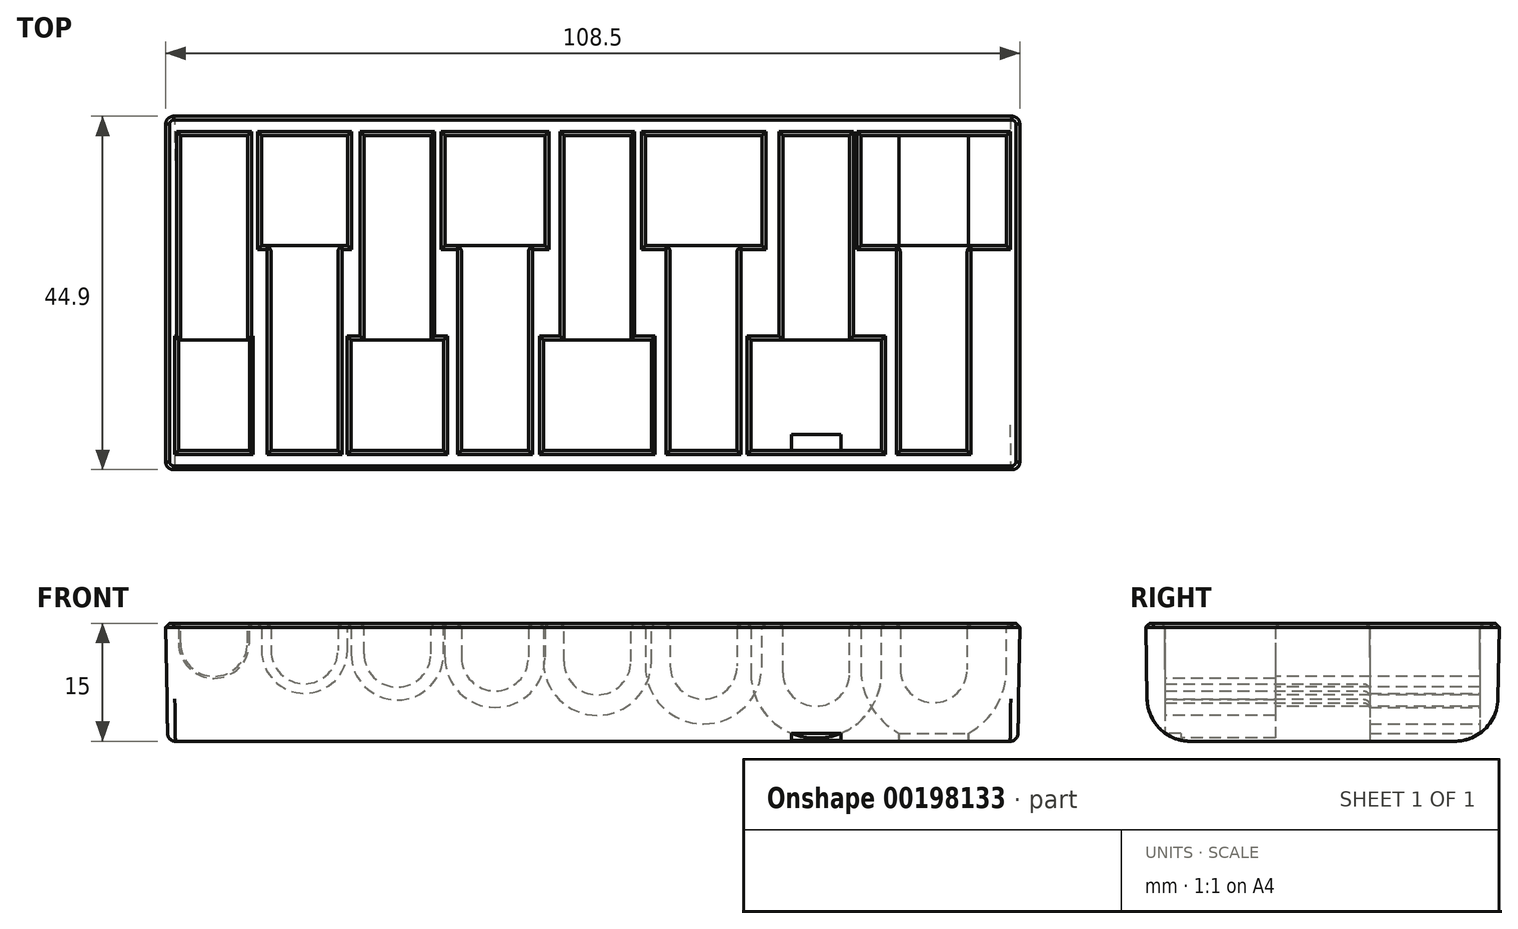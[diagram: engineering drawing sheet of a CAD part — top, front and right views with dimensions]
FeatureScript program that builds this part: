
annotation { "Feature Type Name" : "Feature", "Feature Type Description" : "" }
export const myFeature = defineFeature(function(context is Context, id is Id, definition is map)
    precondition{}
    {
        {
            var Q0;
            Q0=qCreatedBy(makeId("Top.planeOp"),FACE);
            var sketch = newSketch(context, id + "F0", { "sketchPlane" : qUnion([Q0])});
            skLineSegment(sketch, "E0.bottom", {"start": v(54, 22.2) * mm, "end": v(-54, 22.2) * mm});
            skLineSegment(sketch, "E0.top", {"start": v(54, -22.2) * mm, "end": v(-54, -22.2) * mm});
            skLineSegment(sketch, "E0.left", {"start": v(54, 22.2) * mm, "end": v(54, -22.2) * mm});
            skLineSegment(sketch, "E0.right", {"start": v(-54, 22.2) * mm, "end": v(-54, -22.2) * mm});
            skPoint(sketch, "E0.middle", {"position": v(0, 0) * mm});
            skSolve(sketch);
        }
        {
            var Q0;
            Q0=makeQuery(id+"F0.imprint","IMPRINT",FACE,{"disambiguationData":[TD([[makeQuery(id+"F0.imprint","IMPRINT",EDGE,{"derivedFrom":sQuery(id+"F0.wireOp",EDGE,"E0.bottom")}),1.0]])]});
            extrude(context, id + "F1", {"entities" : qUnion([Q0]), "depth" : 15 * mm, "hasDraft" : true, "draftAngle" : 1 * degree});
        }
        {
            var Q0;
            Q0=makeQuery(id+"F1.opExtrude","CAP_EDGE",EDGE,{"disambiguationData":[OSD([sQuery(id+"F0.wireOp",EDGE,"E0.top")])],"isStart":true});
            var Q1;
            Q1=makeQuery(id+"F1.opExtrude","CAP_EDGE",EDGE,{"disambiguationData":[OSD([sQuery(id+"F0.wireOp",EDGE,"E0.bottom")])],"isStart":true});
            fillet(context, id + "F2", {"entities" : qUnion([Q0, Q1]), "radius" : 5.5 * mm, "tangentPropagation" : true, "allowEdgeOverflow" : false});
        }
        {
            var Q0;
            Q0=makeQuery(id+"F1.opExtrude","SWEPT_EDGE",EDGE,{"disambiguationData":[OSD([sQuery(id+"F0.wireOp",EDGE,"E0.top"),sQuery(id+"F0.wireOp",EDGE,"E0.left")])]});
            var Q1;
            Q1=makeQuery(id+"F1.opExtrude","SWEPT_EDGE",EDGE,{"disambiguationData":[OSD([sQuery(id+"F0.wireOp",EDGE,"E0.top"),sQuery(id+"F0.wireOp",EDGE,"E0.right")])]});
            fillet(context, id + "F3", {"entities" : qUnion([Q0, Q1]), "radius" : 1 * mm, "tangentPropagation" : true, "allowEdgeOverflow" : false});
        }
        {
            var Q0;
            Q0=qCreatedBy(makeId("Front.planeOp"),FACE);
            cPlane(context, id + "F4", {"entities" : qUnion([Q0]), "cplaneType" : CPlaneType.OFFSET, "offset" : 20 * mm, "width" : 150 * mm, "height" : 150 * mm});
        }
        {
            var Q0;
            Q0=qCreatedBy(makeId("Front.planeOp"),FACE);
            cPlane(context, id + "F5", {"entities" : qUnion([Q0]), "cplaneType" : CPlaneType.OFFSET, "offset" : 20 * mm, "oppositeDirection" : true, "width" : 150 * mm, "height" : 150 * mm});
        }
        {
            var Q0;
            Q0=qCreatedBy(id+"F5.planeOp",FACE);
            var sketch = newSketch(context, id + "F6", { "sketchPlane" : qUnion([Q0])});
            skLineSegment(sketch, "E1", {"start": v(0, 0) * mm, "end": v(0, 15) * mm, "construction": true});
            skPoint(sketch, "E2.0", {"position": v(54.26, 15) * mm});
            skArc(sketch, "E3.0", {"start": v(-53.02, 0) * mm, "mid": v(-53.72, 0.29) * mm, "end": v(-54.02, 0.98) * mm, "construction": true});
            skLineSegment(sketch, "E4.0", {"start": v(53.26, 15) * mm, "end": v(-53.26, 15) * mm, "construction": true});
            skArc(sketch, "E5", {"start": v(34.06, 9.15) * mm, "mid": v(43.3, -0.1) * mm, "end": v(52.56, 9.15) * mm});
            skArc(sketch, "E6", {"start": v(39.06, 9.15) * mm, "mid": v(43.3, 4.9) * mm, "end": v(47.56, 9.15) * mm});
            skLineSegment(sketch, "E7.0", {"start": v(-53.02, 0) * mm, "end": v(53.02, 0) * mm, "construction": true});
            skCircle(sketch, "E8", {"center": v(28.38, 8.7) * mm, "radius": 8.3 * mm, "construction": true});
            skCircle(sketch, "E9", {"center": v(28.38, 8.7) * mm, "radius": 4.25 * mm, "construction": true});
            skArc(sketch, "E10", {"start": v(20.94, 12.38) * mm, "mid": v(13.96, 17) * mm, "end": v(7.13, 12.15) * mm, "construction": true});
            skArc(sketch, "E11", {"start": v(9.83, 9.6) * mm, "mid": v(14.08, 5.35) * mm, "end": v(18.33, 9.6) * mm});
            skCircle(sketch, "E12", {"center": v(0.58, 10.15) * mm, "radius": 6.85 * mm, "construction": true});
            skCircle(sketch, "E13", {"center": v(0.58, 10.15) * mm, "radius": 4.25 * mm, "construction": true});
            skArc(sketch, "E14", {"start": v(-6.13, 11.53) * mm, "mid": v(-12.16, 17) * mm, "end": v(-18.61, 12.04) * mm, "construction": true});
            skArc(sketch, "E15", {"start": v(-16.67, 10.65) * mm, "mid": v(-12.42, 6.4) * mm, "end": v(-8.17, 10.65) * mm});
            skCircle(sketch, "E16", {"center": v(-24.82, 11.12) * mm, "radius": 5.88 * mm, "construction": true});
            skCircle(sketch, "E17", {"center": v(-24.82, 11.12) * mm, "radius": 4.25 * mm, "construction": true});
            skArc(sketch, "E18", {"start": v(-31.28, 12.67) * mm, "mid": v(-35.33, 16.85) * mm, "end": v(-40.84, 15) * mm, "construction": true});
            skArc(sketch, "E19", {"start": v(-40.87, 11.55) * mm, "mid": v(-36.62, 7.3) * mm, "end": v(-32.37, 11.55) * mm});
            skCircle(sketch, "E20", {"center": v(-48.12, 12.5) * mm, "radius": 4.5 * mm, "construction": true});
            skCircle(sketch, "E21", {"center": v(-48.12, 12.5) * mm, "radius": 4.25 * mm, "construction": true});
            skLineSegment(sketch, "E22", {"start": v(55.71, 17) * mm, "end": v(-54.74, 17) * mm, "construction": true});
            skLineSegment(sketch, "E23", {"start": v(52.56, 9.15) * mm, "end": v(52.56, 15) * mm});
            skLineSegment(sketch, "E24", {"start": v(52.56, 15) * mm, "end": v(34.06, 15) * mm});
            skLineSegment(sketch, "E25", {"start": v(34.06, 15) * mm, "end": v(34.06, 9.15) * mm});
            skLineSegment(sketch, "E26", {"start": v(36.68, 8.7) * mm, "end": v(36.68, 15) * mm, "construction": true});
            skLineSegment(sketch, "E27", {"start": v(36.68, 15) * mm, "end": v(20.08, 15) * mm});
            skLineSegment(sketch, "E28", {"start": v(20.08, 15) * mm, "end": v(20.08, 8.7) * mm, "construction": true});
            skLineSegment(sketch, "E29", {"start": v(21.48, 9.6) * mm, "end": v(21.48, 15) * mm});
            skLineSegment(sketch, "E30", {"start": v(21.48, 15) * mm, "end": v(6.68, 15) * mm});
            skLineSegment(sketch, "E31", {"start": v(6.68, 15) * mm, "end": v(6.68, 9.6) * mm});
            skArc(sketch, "E32.trimOffspring", {"start": v(50.47, 15) * mm, "mid": v(42.41, 18.36) * mm, "end": v(35.15, 13.5) * mm, "construction": true});
            skArc(sketch, "E33.trimOffspring", {"start": v(6.68, 9.6) * mm, "mid": v(14.08, 2.2) * mm, "end": v(21.48, 9.6) * mm});
            skLineSegment(sketch, "E34", {"start": v(6.68, 15) * mm, "end": v(21.48, 15) * mm});
            skLineSegment(sketch, "E35", {"start": v(34.06, 15) * mm, "end": v(52.56, 15) * mm});
            skLineSegment(sketch, "E36", {"start": v(7.43, 10.15) * mm, "end": v(7.43, 15) * mm, "construction": true});
            skLineSegment(sketch, "E37", {"start": v(7.43, 15) * mm, "end": v(-6.27, 15) * mm, "construction": true});
            skLineSegment(sketch, "E38", {"start": v(-6.27, 15) * mm, "end": v(-6.27, 10.15) * mm, "construction": true});
            skLineSegment(sketch, "E39", {"start": v(-18.77, 10.65) * mm, "end": v(-18.77, 15) * mm});
            skLineSegment(sketch, "E40", {"start": v(-18.77, 15) * mm, "end": v(-6.07, 15) * mm});
            skLineSegment(sketch, "E41", {"start": v(-6.07, 15) * mm, "end": v(-6.07, 10.65) * mm});
            skPoint(sketch, "E42.orphan", {"position": v(-6.07, 10.15) * mm});
            skArc(sketch, "E43.trimOffspring", {"start": v(-18.77, 10.65) * mm, "mid": v(-12.42, 4.3) * mm, "end": v(-6.07, 10.65) * mm});
            skLineSegment(sketch, "E44", {"start": v(-18.77, 15) * mm, "end": v(-6.07, 15) * mm, "construction": true});
            skLineSegment(sketch, "E45", {"start": v(-18.94, 11.12) * mm, "end": v(-18.94, 15) * mm, "construction": true});
            skLineSegment(sketch, "E46", {"start": v(-18.94, 15) * mm, "end": v(-30.7, 15) * mm, "construction": true});
            skLineSegment(sketch, "E47", {"start": v(-30.7, 15) * mm, "end": v(-30.7, 11.12) * mm, "construction": true});
            skLineSegment(sketch, "E48", {"start": v(-31.17, 11.55) * mm, "end": v(-31.17, 15) * mm});
            skLineSegment(sketch, "E49", {"start": v(-31.17, 15) * mm, "end": v(-42.07, 15) * mm});
            skLineSegment(sketch, "E50", {"start": v(-42.07, 15) * mm, "end": v(-42.07, 11.55) * mm});
            skArc(sketch, "E51.trimOffspring", {"start": v(-42.07, 11.55) * mm, "mid": v(-36.62, 6.1) * mm, "end": v(-31.17, 11.55) * mm});
            skLineSegment(sketch, "E52", {"start": v(-31.17, 15) * mm, "end": v(-42.07, 15) * mm, "construction": true});
            skLineSegment(sketch, "E53", {"start": v(-43.62, 12.5) * mm, "end": v(-43.62, 15) * mm, "construction": true});
            skLineSegment(sketch, "E54", {"start": v(-43.62, 15) * mm, "end": v(-52.62, 15) * mm, "construction": true});
            skLineSegment(sketch, "E55", {"start": v(-52.62, 15) * mm, "end": v(-52.62, 12.5) * mm, "construction": true});
            skLineSegment(sketch, "E56", {"start": v(-34.14, 15) * mm, "end": v(-39.1, 15) * mm});
            skLineSegment(sketch, "E57.top", {"start": v(47.56, 15) * mm, "end": v(39.06, 15) * mm});
            skLineSegment(sketch, "E57.left", {"start": v(47.56, 9.15) * mm, "end": v(47.56, 15) * mm});
            skLineSegment(sketch, "E57.right", {"start": v(39.06, 9.15) * mm, "end": v(39.06, 15) * mm});
            skLineSegment(sketch, "E58.bottom", {"start": v(32.63, 8.7) * mm, "end": v(24.13, 8.7) * mm, "construction": true});
            skLineSegment(sketch, "E58.top", {"start": v(32.63, 15) * mm, "end": v(24.13, 15) * mm, "construction": true});
            skLineSegment(sketch, "E58.left", {"start": v(32.63, 8.7) * mm, "end": v(32.63, 15) * mm, "construction": true});
            skLineSegment(sketch, "E58.right", {"start": v(24.13, 8.7) * mm, "end": v(24.13, 15) * mm, "construction": true});
            skLineSegment(sketch, "E59.top", {"start": v(18.33, 15) * mm, "end": v(9.83, 15) * mm});
            skLineSegment(sketch, "E59.left", {"start": v(18.33, 9.6) * mm, "end": v(18.33, 15) * mm});
            skLineSegment(sketch, "E59.right", {"start": v(9.83, 9.6) * mm, "end": v(9.83, 15) * mm});
            skLineSegment(sketch, "E60.bottom", {"start": v(4.83, 10.15) * mm, "end": v(-3.67, 10.15) * mm, "construction": true});
            skLineSegment(sketch, "E60.top", {"start": v(4.83, 15) * mm, "end": v(-3.67, 15) * mm, "construction": true});
            skLineSegment(sketch, "E60.left", {"start": v(4.83, 10.15) * mm, "end": v(4.83, 15) * mm, "construction": true});
            skLineSegment(sketch, "E60.right", {"start": v(-3.67, 10.15) * mm, "end": v(-3.67, 15) * mm, "construction": true});
            skLineSegment(sketch, "E61.top", {"start": v(-8.17, 15) * mm, "end": v(-16.67, 15) * mm});
            skLineSegment(sketch, "E61.left", {"start": v(-8.17, 10.65) * mm, "end": v(-8.17, 15) * mm});
            skLineSegment(sketch, "E61.right", {"start": v(-16.67, 10.65) * mm, "end": v(-16.67, 15) * mm});
            skLineSegment(sketch, "E62.bottom", {"start": v(-20.57, 11.12) * mm, "end": v(-29.07, 11.12) * mm, "construction": true});
            skLineSegment(sketch, "E62.top", {"start": v(-20.57, 15) * mm, "end": v(-29.07, 15) * mm, "construction": true});
            skLineSegment(sketch, "E62.left", {"start": v(-20.57, 11.12) * mm, "end": v(-20.57, 15) * mm, "construction": true});
            skLineSegment(sketch, "E62.right", {"start": v(-29.07, 11.12) * mm, "end": v(-29.07, 15) * mm, "construction": true});
            skLineSegment(sketch, "E63.top", {"start": v(-32.37, 15) * mm, "end": v(-40.87, 15) * mm});
            skLineSegment(sketch, "E63.left", {"start": v(-32.37, 11.55) * mm, "end": v(-32.37, 15) * mm});
            skLineSegment(sketch, "E63.right", {"start": v(-40.87, 11.55) * mm, "end": v(-40.87, 15) * mm});
            skLineSegment(sketch, "E64.bottom", {"start": v(-43.87, 12.5) * mm, "end": v(-52.37, 12.5) * mm, "construction": true});
            skLineSegment(sketch, "E64.top", {"start": v(-43.87, 15) * mm, "end": v(-52.37, 15) * mm, "construction": true});
            skLineSegment(sketch, "E64.left", {"start": v(-43.87, 12.5) * mm, "end": v(-43.87, 15) * mm, "construction": true});
            skLineSegment(sketch, "E64.right", {"start": v(-52.37, 12.5) * mm, "end": v(-52.37, 15) * mm, "construction": true});
            skSolve(sketch);
        }
        {
            var Q0;
            Q0=makeQuery(id+"F6.imprint","IMPRINT",FACE,{"disambiguationData":[TD([[makeQuery(id+"F6.imprint","IMPRINT",EDGE,{"derivedFrom":sQuery(id+"F6.wireOp",EDGE,"E6")}),1.0]])]});
            var Q1;
            Q1=makeQuery(id+"F6.imprint","IMPRINT",FACE,{"disambiguationData":[TD([[makeQuery(id+"F6.imprint","IMPRINT",EDGE,{"derivedFrom":sQuery(id+"F6.wireOp",EDGE,"E11")}),-1.0]])]});
            var Q2;
            Q2=makeQuery(id+"F6.imprint","IMPRINT",FACE,{"disambiguationData":[TD([[makeQuery(id+"F6.imprint","IMPRINT",EDGE,{"derivedFrom":sQuery(id+"F6.wireOp",EDGE,"E11")}),1.0]])]});
            var Q3;
            Q3=makeQuery(id+"F6.imprint","IMPRINT",FACE,{"disambiguationData":[TD([[makeQuery(id+"F6.imprint","IMPRINT",EDGE,{"derivedFrom":sQuery(id+"F6.wireOp",EDGE,"E15")}),-1.0]])]});
            var Q4;
            Q4=makeQuery(id+"F6.imprint","IMPRINT",FACE,{"disambiguationData":[TD([[makeQuery(id+"F6.imprint","IMPRINT",EDGE,{"derivedFrom":sQuery(id+"F6.wireOp",EDGE,"E15")}),1.0]])]});
            var Q5;
            {var subQ2=sQuery(id+"F6.wireOp",EDGE,"E19");Q5=makeQuery(id+"F6.imprint","IMPRINT",FACE,{"disambiguationData":[TD([[makeQuery(id+"F6.imprint","IMPRINT",EDGE,{"derivedFrom":subQ2}),-1.0]])]});}
            var Q6;
            Q6=makeQuery(id+"F6.imprint","IMPRINT",FACE,{"disambiguationData":[TD([[makeQuery(id+"F6.imprint","IMPRINT",EDGE,{"derivedFrom":sQuery(id+"F6.wireOp",EDGE,"E19")}),1.0]])]});
            var Q7;
            Q7=makeQuery(id+"F6.imprint","IMPRINT",FACE,{"disambiguationData":[TD([[makeQuery(id+"F6.imprint","IMPRINT",EDGE,{"derivedFrom":sQuery(id+"F6.wireOp",EDGE,"E5")}),1.0]])]});
            extrude(context, id + "F7", {"entities" : qUnion([Q0, Q1, Q2, Q3, Q4, Q5, Q6, Q7]), "operationType" : NewBodyOperationType.REMOVE, "depth" : 14 * mm});
        }
        {
            var Q0;
            Q0=makeQuery(id+"F6.imprint","IMPRINT",FACE,{"disambiguationData":[TD([[makeQuery(id+"F6.imprint","IMPRINT",EDGE,{"derivedFrom":sQuery(id+"F6.wireOp",EDGE,"E6")}),1.0]])]});
            var Q1;
            Q1=makeQuery(id+"F6.imprint","IMPRINT",FACE,{"disambiguationData":[TD([[makeQuery(id+"F6.imprint","IMPRINT",EDGE,{"derivedFrom":sQuery(id+"F6.wireOp",EDGE,"E11")}),1.0]])]});
            var Q2;
            Q2=makeQuery(id+"F6.imprint","IMPRINT",FACE,{"disambiguationData":[TD([[makeQuery(id+"F6.imprint","IMPRINT",EDGE,{"derivedFrom":sQuery(id+"F6.wireOp",EDGE,"E15")}),1.0]])]});
            var Q3;
            Q3=makeQuery(id+"F6.imprint","IMPRINT",FACE,{"disambiguationData":[TD([[makeQuery(id+"F6.imprint","IMPRINT",EDGE,{"derivedFrom":sQuery(id+"F6.wireOp",EDGE,"E19")}),1.0]])]});
            var Q4;
            Q4=qCreatedBy(id+"F4.planeOp",FACE);
            extrude(context, id + "F8", {"entities" : qUnion([Q0, Q1, Q2, Q3]), "operationType" : NewBodyOperationType.REMOVE, "endBound" : BoundingType.UP_TO_SURFACE, "endBoundEntityFace" : qUnion([Q4]), "depth" : 27 * mm});
        }
        {
            var Q0;
            Q0=qCreatedBy(id+"F4.planeOp",FACE);
            var sketch = newSketch(context, id + "F9", { "sketchPlane" : qUnion([Q0])});
            skLineSegment(sketch, "E65.0", {"start": v(32.63, 8.7) * mm, "end": v(32.63, 15) * mm});
            skArc(sketch, "E66.0", {"start": v(24.13, 8.7) * mm, "mid": v(28.38, 4.45) * mm, "end": v(32.63, 8.7) * mm});
            skLineSegment(sketch, "E67.0", {"start": v(24.13, 8.7) * mm, "end": v(24.13, 15) * mm});
            skArc(sketch, "E68.0", {"start": v(20.08, 8.7) * mm, "mid": v(28.38, 0.4) * mm, "end": v(36.68, 8.7) * mm});
            skLineSegment(sketch, "E69.0", {"start": v(20.08, 15) * mm, "end": v(20.08, 8.7) * mm});
            skLineSegment(sketch, "E70.0", {"start": v(36.68, 15) * mm, "end": v(20.08, 15) * mm});
            skLineSegment(sketch, "E71.0", {"start": v(36.68, 8.7) * mm, "end": v(36.68, 15) * mm});
            skPoint(sketch, "E72.orphan", {"position": v(34.06, 15) * mm});
            skPoint(sketch, "E73.0.end.orphan", {"position": v(34.06, 9.15) * mm});
            skArc(sketch, "E74.0", {"start": v(-3.67, 10.15) * mm, "mid": v(0.58, 5.9) * mm, "end": v(4.83, 10.15) * mm});
            skLineSegment(sketch, "E75.0", {"start": v(4.83, 10.15) * mm, "end": v(4.83, 15) * mm});
            skLineSegment(sketch, "E76.0", {"start": v(-3.67, 10.15) * mm, "end": v(-3.67, 15) * mm});
            skArc(sketch, "E77.0", {"start": v(-6.27, 10.15) * mm, "mid": v(0.58, 3.3) * mm, "end": v(7.43, 10.15) * mm});
            skLineSegment(sketch, "E78.0", {"start": v(7.43, 10.15) * mm, "end": v(7.43, 15) * mm});
            skLineSegment(sketch, "E79.0", {"start": v(-6.27, 15) * mm, "end": v(-6.27, 10.15) * mm});
            skLineSegment(sketch, "E80", {"start": v(-6.27, 15) * mm, "end": v(7.43, 15) * mm});
            skArc(sketch, "E81.0", {"start": v(-30.7, 11.12) * mm, "mid": v(-24.82, 5.25) * mm, "end": v(-18.94, 11.12) * mm});
            skArc(sketch, "E82.0", {"start": v(-29.07, 11.12) * mm, "mid": v(-24.82, 6.87) * mm, "end": v(-20.57, 11.12) * mm});
            skLineSegment(sketch, "E83.0", {"start": v(-20.57, 11.12) * mm, "end": v(-20.57, 15) * mm});
            skLineSegment(sketch, "E84.0", {"start": v(-29.07, 11.12) * mm, "end": v(-29.07, 15) * mm});
            skLineSegment(sketch, "E85.0", {"start": v(-18.94, 11.12) * mm, "end": v(-18.94, 15) * mm});
            skLineSegment(sketch, "E86.0", {"start": v(-30.7, 15) * mm, "end": v(-30.7, 11.12) * mm});
            skLineSegment(sketch, "E87", {"start": v(-30.7, 15) * mm, "end": v(-18.94, 15) * mm});
            skArc(sketch, "E88.0", {"start": v(-52.62, 12.5) * mm, "mid": v(-48.12, 8) * mm, "end": v(-43.62, 12.5) * mm});
            skArc(sketch, "E89.0", {"start": v(-52.37, 12.5) * mm, "mid": v(-48.12, 8.25) * mm, "end": v(-43.87, 12.5) * mm});
            skLineSegment(sketch, "E90.0", {"start": v(-43.87, 12.5) * mm, "end": v(-43.87, 15) * mm});
            skLineSegment(sketch, "E91.0", {"start": v(-52.37, 12.5) * mm, "end": v(-52.37, 15) * mm});
            skLineSegment(sketch, "E92.0", {"start": v(-52.62, 15) * mm, "end": v(-52.62, 12.5) * mm});
            skLineSegment(sketch, "E93.0", {"start": v(-43.62, 12.5) * mm, "end": v(-43.62, 15) * mm});
            skLineSegment(sketch, "E94", {"start": v(-43.62, 15) * mm, "end": v(-52.62, 15) * mm});
            skSolve(sketch);
        }
        {
            var Q0;
            Q0=makeQuery(id+"F9.imprint","IMPRINT",FACE,{"disambiguationData":[TD([[makeQuery(id+"F9.imprint","IMPRINT",EDGE,{"derivedFrom":sQuery(id+"F9.wireOp",EDGE,"E88.0")}),1.0]])]});
            var Q1;
            Q1=makeQuery(id+"F9.imprint","IMPRINT",FACE,{"disambiguationData":[TD([[makeQuery(id+"F9.imprint","IMPRINT",EDGE,{"derivedFrom":sQuery(id+"F9.wireOp",EDGE,"E81.0")}),1.0]])]});
            var Q2;
            Q2=makeQuery(id+"F9.imprint","IMPRINT",FACE,{"disambiguationData":[TD([[makeQuery(id+"F9.imprint","IMPRINT",EDGE,{"derivedFrom":sQuery(id+"F9.wireOp",EDGE,"E74.0")}),-1.0]])]});
            var Q3;
            {var subQ1=sQuery(id+"F9.wireOp",EDGE,"E65.0");Q3=makeQuery(id+"F9.imprint","IMPRINT",FACE,{"disambiguationData":[TD([[makeQuery(id+"F9.imprint","IMPRINT",EDGE,{"derivedFrom":subQ1}),-1.0]])]});}
            extrude(context, id + "F10", {"entities" : qUnion([Q0, Q1, Q2, Q3]), "operationType" : NewBodyOperationType.REMOVE, "oppositeDirection" : true, "depth" : 14 * mm});
        }
        {
            var Q0;
            {var subQ0=sQuery(id+"F9.wireOp",EDGE,"E65.0");Q0=makeQuery(id+"F9.imprint","IMPRINT",FACE,{"disambiguationData":[TD([[makeQuery(id+"F9.imprint","IMPRINT",EDGE,{"derivedFrom":subQ0}),1.0]])]});}
            var Q1;
            Q1=makeQuery(id+"F9.imprint","IMPRINT",FACE,{"disambiguationData":[TD([[makeQuery(id+"F9.imprint","IMPRINT",EDGE,{"derivedFrom":sQuery(id+"F9.wireOp",EDGE,"E74.0")}),1.0]])]});
            var Q2;
            Q2=makeQuery(id+"F9.imprint","IMPRINT",FACE,{"disambiguationData":[TD([[makeQuery(id+"F9.imprint","IMPRINT",EDGE,{"derivedFrom":sQuery(id+"F9.wireOp",EDGE,"E82.0")}),1.0]])]});
            var Q3;
            Q3=makeQuery(id+"F9.imprint","IMPRINT",FACE,{"disambiguationData":[TD([[makeQuery(id+"F9.imprint","IMPRINT",EDGE,{"derivedFrom":sQuery(id+"F9.wireOp",EDGE,"E89.0")}),1.0]])]});
            var Q4;
            Q4=qCreatedBy(id+"F5.planeOp",FACE);
            extrude(context, id + "F11", {"entities" : qUnion([Q0, Q1, Q2, Q3]), "operationType" : NewBodyOperationType.REMOVE, "endBound" : BoundingType.UP_TO_SURFACE, "oppositeDirection" : true, "endBoundEntityFace" : qUnion([Q4]), "depth" : 25 * mm});
        }
        {
            var Q0;
            Q0=makeQuery(id+"F1.opExtrude","CAP_FACE",FACE,{"disambiguationData":[OSD([sQuery(id+"F0.wireOp",EDGE,"E0.bottom"),sQuery(id+"F0.wireOp",EDGE,"E0.top"),sQuery(id+"F0.wireOp",EDGE,"E0.left"),sQuery(id+"F0.wireOp",EDGE,"E0.right")])],"isStart":true});
            var sketch = newSketch(context, id + "F12", { "sketchPlane" : qUnion([Q0])});
            skLineSegment(sketch, "E95.0", {"start": v(47.74, -20) * mm, "end": v(38.88, -20) * mm, "construction": true});
            skLineSegment(sketch, "E96.0", {"start": v(41.95, -6) * mm, "end": v(44.66, -6) * mm, "construction": true});
            skLineSegment(sketch, "E97.0", {"start": v(31.55, 20) * mm, "end": v(25.21, 20) * mm, "construction": true});
            skPoint(sketch, "E98.oppositeSnap0", {"position": v(43.3, -6) * mm});
            skLineSegment(sketch, "E98.bottom", {"start": v(47.74, -20) * mm, "end": v(38.88, -20) * mm});
            skLineSegment(sketch, "E98.top", {"start": v(47.74, -6) * mm, "end": v(38.88, -6) * mm});
            skLineSegment(sketch, "E98.left", {"start": v(47.74, -20) * mm, "end": v(47.74, -6) * mm});
            skLineSegment(sketch, "E98.right", {"start": v(38.88, -20) * mm, "end": v(38.88, -6) * mm});
            skLineSegment(sketch, "E99.bottom", {"start": v(31.55, 20) * mm, "end": v(25.21, 20) * mm});
            skLineSegment(sketch, "E99.top", {"start": v(31.55, 18) * mm, "end": v(25.21, 18) * mm});
            skLineSegment(sketch, "E99.left", {"start": v(31.55, 20) * mm, "end": v(31.55, 18) * mm});
            skLineSegment(sketch, "E99.right", {"start": v(25.21, 20) * mm, "end": v(25.21, 18) * mm});
            skSolve(sketch);
        }
        {
            var Q0;
            Q0 = qSketchRegion(id + "F12", true);
            extrude(context, id + "F13", {"entities" : qUnion([Q0]), "operationType" : NewBodyOperationType.REMOVE, "endBound" : BoundingType.THROUGH_ALL, "oppositeDirection" : true, "depth" : 25 * mm});
        }
        {
            var Q0;
            Q0=makeQuery(id+"F1.opExtrude","CAP_FACE",FACE,{"disambiguationData":[OSD([sQuery(id+"F0.wireOp",EDGE,"E0.bottom"),sQuery(id+"F0.wireOp",EDGE,"E0.top"),sQuery(id+"F0.wireOp",EDGE,"E0.left"),sQuery(id+"F0.wireOp",EDGE,"E0.right")])],"isStart":false});
            chamfer(context, id + "F14", {"entities" : qUnion([Q0]), "width" : .5 * mm, "tangentPropagation" : true});
        }
        {
            var Q0;
            Q0=makeQuery(id+"F8.boolean.opBoolean","INTERSECT",EDGE,{"derivedFrom":[makeQuery(id+"F7.boolean.opBoolean","COPY",FACE,{"derivedFrom":makeQuery(id+"F7.opExtrude","CAP_FACE",FACE,{"disambiguationData":[OSD([sQuery(id+"F6.wireOp",EDGE,"E48"),sQuery(id+"F6.wireOp",EDGE,"E49"),sQuery(id+"F6.wireOp",EDGE,"E50"),sQuery(id+"F6.wireOp",EDGE,"E51.trimOffspring"),sQuery(id+"F6.wireOp",EDGE,"E63.top")])],"isStart":false})}),makeQuery(id+"F8.opExtrude","SWEPT_FACE",FACE,{"disambiguationData":[OSD([sQuery(id+"F6.wireOp",EDGE,"E19")])]})]});
            var Q1;
            Q1=makeQuery(id+"F10.boolean.opBoolean","COPY",EDGE,{"derivedFrom":makeQuery(id+"F10.opExtrude","CAP_EDGE",EDGE,{"disambiguationData":[OSD([sQuery(id+"F9.wireOp",EDGE,"E82.0")])],"isStart":false})});
            var Q2;
            Q2=makeQuery(id+"F8.boolean.opBoolean","INTERSECT",EDGE,{"derivedFrom":[makeQuery(id+"F7.boolean.opBoolean","COPY",FACE,{"derivedFrom":makeQuery(id+"F7.opExtrude","CAP_FACE",FACE,{"disambiguationData":[OSD([sQuery(id+"F6.wireOp",EDGE,"E39"),sQuery(id+"F6.wireOp",EDGE,"E40"),sQuery(id+"F6.wireOp",EDGE,"E41"),sQuery(id+"F6.wireOp",EDGE,"E43.trimOffspring"),sQuery(id+"F6.wireOp",EDGE,"E61.top")])],"isStart":false})}),makeQuery(id+"F8.opExtrude","SWEPT_FACE",FACE,{"disambiguationData":[OSD([sQuery(id+"F6.wireOp",EDGE,"E15")])]})]});
            var Q3;
            Q3=makeQuery(id+"F10.boolean.opBoolean","COPY",EDGE,{"derivedFrom":makeQuery(id+"F10.opExtrude","CAP_EDGE",EDGE,{"disambiguationData":[OSD([sQuery(id+"F9.wireOp",EDGE,"E74.0")])],"isStart":false})});
            var Q4;
            Q4=makeQuery(id+"F8.boolean.opBoolean","INTERSECT",EDGE,{"derivedFrom":[makeQuery(id+"F7.boolean.opBoolean","COPY",FACE,{"derivedFrom":makeQuery(id+"F7.opExtrude","CAP_FACE",FACE,{"disambiguationData":[OSD([sQuery(id+"F6.wireOp",EDGE,"E29"),sQuery(id+"F6.wireOp",EDGE,"E31"),sQuery(id+"F6.wireOp",EDGE,"E33.trimOffspring"),sQuery(id+"F6.wireOp",EDGE,"E34"),sQuery(id+"F6.wireOp",EDGE,"E59.top")])],"isStart":false})}),makeQuery(id+"F8.opExtrude","SWEPT_FACE",FACE,{"disambiguationData":[OSD([sQuery(id+"F6.wireOp",EDGE,"E11")])]})]});
            var Q5;
            Q5=makeQuery(id+"F10.boolean.opBoolean","COPY",EDGE,{"derivedFrom":makeQuery(id+"F10.opExtrude","CAP_EDGE",EDGE,{"disambiguationData":[OSD([sQuery(id+"F9.wireOp",EDGE,"E66.0")])],"isStart":false})});
            var Q6;
            Q6=makeQuery(id+"F8.boolean.opBoolean","INTERSECT",EDGE,{"derivedFrom":[makeQuery(id+"F7.boolean.opBoolean","COPY",FACE,{"derivedFrom":makeQuery(id+"F7.opExtrude","CAP_FACE",FACE,{"disambiguationData":[OSD([sQuery(id+"F6.wireOp",EDGE,"E5"),sQuery(id+"F6.wireOp",EDGE,"E23"),sQuery(id+"F6.wireOp",EDGE,"E25"),sQuery(id+"F6.wireOp",EDGE,"E35"),sQuery(id+"F6.wireOp",EDGE,"E57.top")])],"isStart":false})}),makeQuery(id+"F8.opExtrude","SWEPT_FACE",FACE,{"disambiguationData":[OSD([sQuery(id+"F6.wireOp",EDGE,"E6")])]})]});
            var Q7;
            Q7=makeQuery(id+"F10.boolean.opBoolean","COPY",EDGE,{"derivedFrom":makeQuery(id+"F10.opExtrude","CAP_EDGE",EDGE,{"disambiguationData":[OSD([sQuery(id+"F9.wireOp",EDGE,"E89.0")])],"isStart":false})});
            fillet(context, id + "F15", {"entities" : qUnion([Q0, Q1, Q2, Q3, Q4, Q5, Q6, Q7]), "radius" : .8 * mm, "tangentPropagation" : true, "allowEdgeOverflow" : false});
        }
    });
